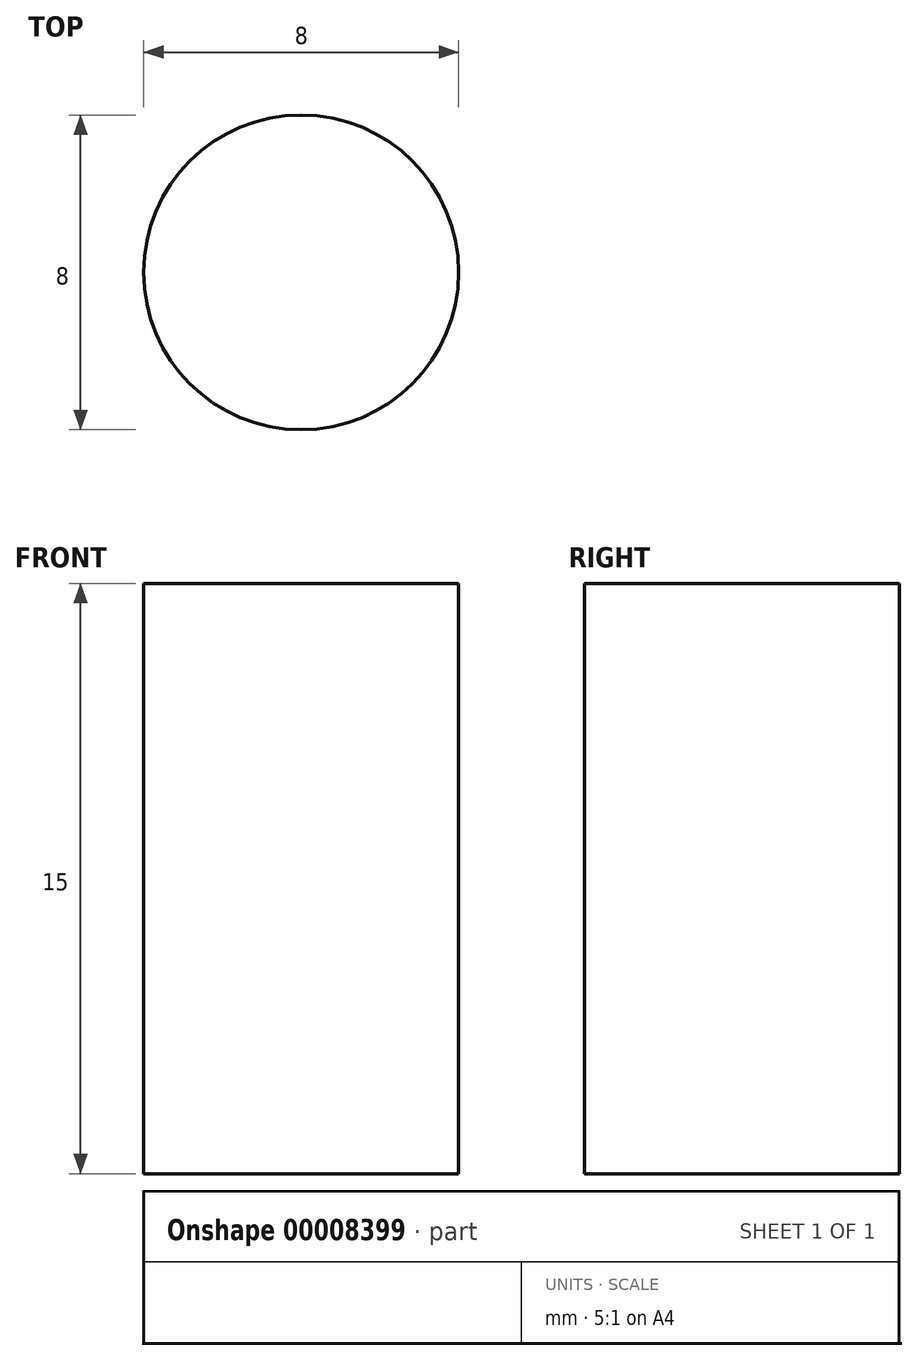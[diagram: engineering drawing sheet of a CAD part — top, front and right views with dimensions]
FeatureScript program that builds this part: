
annotation { "Feature Type Name" : "Feature", "Feature Type Description" : "" }
export const myFeature = defineFeature(function(context is Context, id is Id, definition is map)
    precondition{}
    {
        {
            var Q0;
            Q0=qCreatedBy(makeId("Top.planeOp"),FACE);
            var sketch = newSketch(context, id + "F0", { "sketchPlane" : qUnion([Q0])});
            skCircle(sketch, "E0", {"center": v(0, 0) * mm, "radius": 4 * mm});
            skSolve(sketch);
        }
        {
            var Q0;
            Q0 = qSketchRegion(id + "F0", true);
            extrude(context, id + "F1", {"entities" : qUnion([Q0]), "depth" : 15 * mm});
        }
    });
